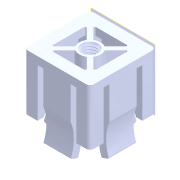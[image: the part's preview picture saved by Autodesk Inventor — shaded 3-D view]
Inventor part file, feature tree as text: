
AUTODESK INVENTOR PART (.ipt)
format: ipt  version: 2021 (Build 250183000, 183)  size: 422,400 bytes
history: native  units: mm
features: plane x1, split x1, other x1
ambient origin geometry x8: Origin, YZ Plane, XZ Plane, XY Plane, X Axis, Y Axis, Z Axis, Center Point
bodies: Solid1 (feature_tree)
feature tree (3):
  plane  "Work Plane1"
  split  "Split1"
  other  "Austragung1"
